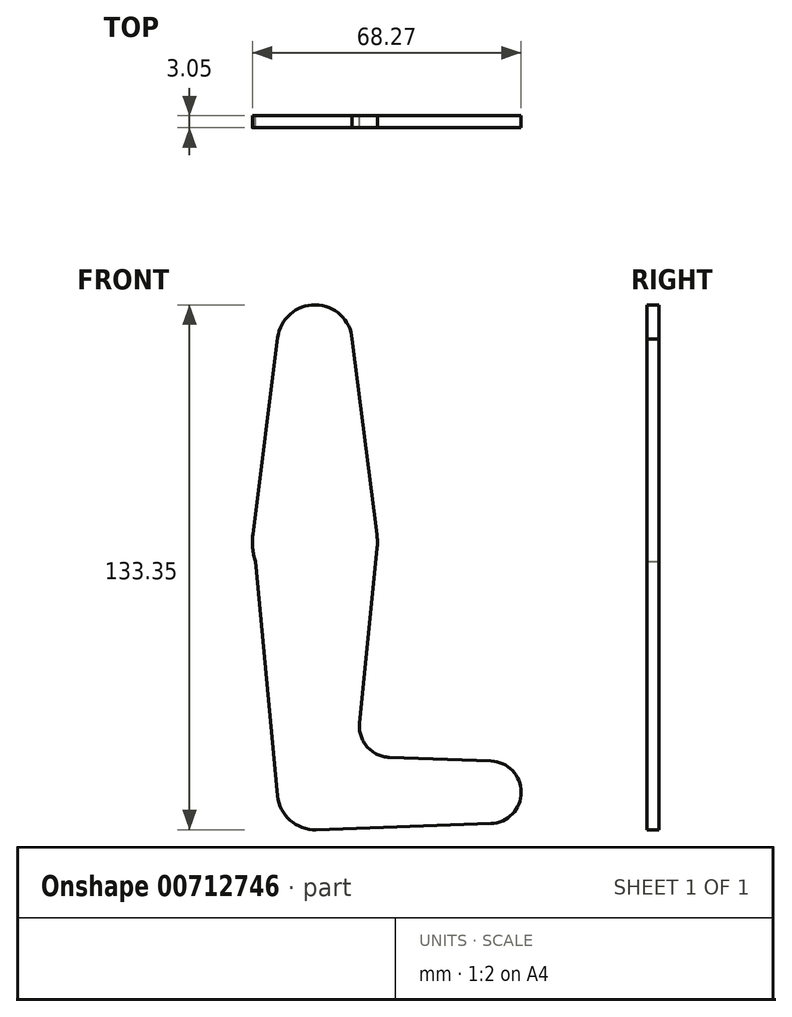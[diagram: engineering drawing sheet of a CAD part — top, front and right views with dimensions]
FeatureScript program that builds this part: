
annotation { "Feature Type Name" : "Feature", "Feature Type Description" : "" }
export const myFeature = defineFeature(function(context is Context, id is Id, definition is map)
    precondition{}
    {
        {
            var Q0;
            Q0=qCreatedBy(makeId("Front.planeOp"),FACE);
            var sketch = newSketch(context, id + "F0", { "sketchPlane" : qUnion([Q0])});
            skLineSegment(sketch, "E0", {"start": v(0, 86.02) * mm, "end": v(0, -28.28) * mm, "construction": true});
            skLineSegment(sketch, "E1", {"start": v(0, -28.28) * mm, "end": v(44.45, -28.28) * mm, "construction": true});
            skCircle(sketch, "E2", {"center": v(0, 86.02) * mm, "radius": 9.53 * mm});
            skCircle(sketch, "E3", {"center": v(0, 35.22) * mm, "radius": 15.88 * mm});
            skCircle(sketch, "E4", {"center": v(0, -28.28) * mm, "radius": 9.53 * mm});
            skCircle(sketch, "E5", {"center": v(44.45, -28.28) * mm, "radius": 7.94 * mm});
            skLineSegment(sketch, "E6", {"start": v(-9.45, 87.21) * mm, "end": v(-15.75, 37.2) * mm});
            skLineSegment(sketch, "E7", {"start": v(9.48, 86.9) * mm, "end": v(15.75, 37.2) * mm});
            skLineSegment(sketch, "E8", {"start": v(-15.75, 37.2) * mm, "end": v(-9.48, -29.17) * mm});
            skLineSegment(sketch, "E9", {"start": v(15.8, 33.64) * mm, "end": v(11.34, -10.68) * mm});
            skLineSegment(sketch, "E10", {"start": v(18.97, -19.42) * mm, "end": v(44.73, -20.34) * mm});
            skLineSegment(sketch, "E11", {"start": v(0.34, -37.8) * mm, "end": v(44.73, -36.2) * mm});
            skCircle(sketch, "E12", {"center": v(0, 35.22) * mm, "radius": 1.59 * mm});
            skCircle(sketch, "E13", {"center": v(0, 86.02) * mm, "radius": 1.59 * mm});
            skCircle(sketch, "E14", {"center": v(0, -28.28) * mm, "radius": 1.59 * mm});
            skCircle(sketch, "E15", {"center": v(44.45, -28.28) * mm, "radius": 1.59 * mm});
            skCircle(sketch, "E16", {"center": v(-6.5, 71.75) * mm, "radius": 1.59 * mm});
            skPoint(sketch, "E17.newPointA", {"position": v(0, -18.75) * mm});
            skPoint(sketch, "E17.newPointB", {"position": v(9.45, -29.55) * mm});
            skArc(sketch, "E17.filletArc", {"start": v(11.34, -10.68) * mm, "mid": v(13.26, -16.7) * mm, "end": v(18.97, -19.42) * mm});
            skSolve(sketch);
        }
        {
            var Q0;
            {var subQ0=sQuery(id+"F0.wireOp",EDGE,"E8");var subQ1=sQuery(id+"F0.wireOp",EDGE,"E3");var subQ3=makeQuery(id+"F0.imprint","INTERSECT",VERTEX,{"derivedFrom":[subQ1,subQ0]});Q0=makeQuery(id+"F0.imprint","IMPRINT",FACE,{"disambiguationData":[TD([[makeQuery(id+"F0.imprint","IMPRINT",EDGE,{"disambiguationData":[TD([[subQ3,1.0]])],"derivedFrom":subQ1}),1.0]])]});}
            var Q1;
            Q1=makeQuery(id+"F0.imprint","IMPRINT",FACE,{"disambiguationData":[TD([[makeQuery(id+"F0.imprint","IMPRINT",EDGE,{"derivedFrom":sQuery(id+"F0.wireOp",EDGE,"E13")}),-1.0]])]});
            var Q2;
            Q2=makeQuery(id+"F0.imprint","IMPRINT",FACE,{"disambiguationData":[TD([[makeQuery(id+"F0.imprint","IMPRINT",EDGE,{"derivedFrom":sQuery(id+"F0.wireOp",EDGE,"E14")}),-1.0]])]});
            var Q3;
            Q3=makeQuery(id+"F0.imprint","IMPRINT",FACE,{"disambiguationData":[TD([[makeQuery(id+"F0.imprint","IMPRINT",EDGE,{"derivedFrom":sQuery(id+"F0.wireOp",EDGE,"E15")}),-1.0]])]});
            var Q4;
            {var subQ0=sQuery(id+"F0.wireOp",EDGE,"E6");Q4=makeQuery(id+"F0.imprint","IMPRINT",FACE,{"disambiguationData":[TD([[makeQuery(id+"F0.imprint","IMPRINT",EDGE,{"derivedFrom":subQ0}),1.0]])]});}
            var Q5;
            {var subQ8=sQuery(id+"F0.wireOp",EDGE,"E9");Q5=makeQuery(id+"F0.imprint","IMPRINT",FACE,{"disambiguationData":[TD([[makeQuery(id+"F0.imprint","IMPRINT",EDGE,{"derivedFrom":subQ8}),-1.0]])]});}
            var Q6;
            Q6=makeQuery(id+"F0.imprint","IMPRINT",FACE,{"disambiguationData":[TD([[makeQuery(id+"F0.imprint","IMPRINT",EDGE,{"derivedFrom":sQuery(id+"F0.wireOp",EDGE,"E12")}),-1.0]])]});
            var Q7;
            Q7=makeQuery(id+"F0.imprint","IMPRINT",FACE,{"disambiguationData":[TD([[makeQuery(id+"F0.imprint","IMPRINT",EDGE,{"derivedFrom":sQuery(id+"F0.wireOp",EDGE,"E16")}),1.0]])]});
            var Q8;
            Q8=makeQuery(id+"F0.imprint","IMPRINT",FACE,{"disambiguationData":[TD([[makeQuery(id+"F0.imprint","IMPRINT",EDGE,{"derivedFrom":sQuery(id+"F0.wireOp",EDGE,"E12")}),1.0]])]});
            var Q9;
            Q9=makeQuery(id+"F0.imprint","IMPRINT",FACE,{"disambiguationData":[TD([[makeQuery(id+"F0.imprint","IMPRINT",EDGE,{"derivedFrom":sQuery(id+"F0.wireOp",EDGE,"E13")}),1.0]])]});
            var Q10;
            Q10=makeQuery(id+"F0.imprint","IMPRINT",FACE,{"disambiguationData":[TD([[makeQuery(id+"F0.imprint","IMPRINT",EDGE,{"derivedFrom":sQuery(id+"F0.wireOp",EDGE,"E15")}),1.0]])]});
            var Q11;
            Q11=makeQuery(id+"F0.imprint","IMPRINT",FACE,{"disambiguationData":[TD([[makeQuery(id+"F0.imprint","IMPRINT",EDGE,{"derivedFrom":sQuery(id+"F0.wireOp",EDGE,"E14")}),1.0]])]});
            extrude(context, id + "F1", {"entities" : qUnion([Q0, Q1, Q2, Q3, Q4, Q5, Q6, Q7, Q8, Q9, Q10, Q11]), "depth" : 3.05 * mm, "offsetDistance" : 25.4 * mm});
        }
    });
